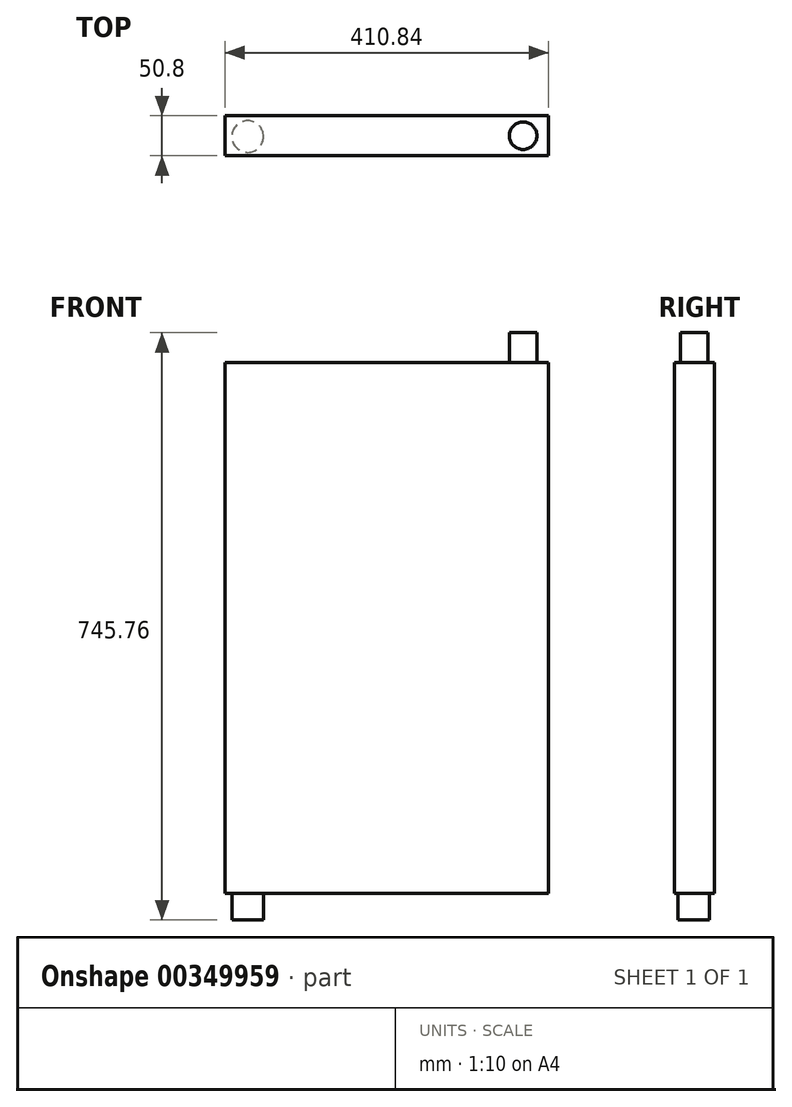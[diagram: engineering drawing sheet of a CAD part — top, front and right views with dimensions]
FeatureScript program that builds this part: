
annotation { "Feature Type Name" : "Feature", "Feature Type Description" : "" }
export const myFeature = defineFeature(function(context is Context, id is Id, definition is map)
    precondition{}
    {
        {
            var Q0;
            Q0=qCreatedBy(makeId("Front.planeOp"),FACE);
            var sketch = newSketch(context, id + "F0", { "sketchPlane" : qUnion([Q0])});
            skLineSegment(sketch, "E0.bottom", {"start": v(205.42, -336.94) * mm, "end": v(-205.42, -336.94) * mm});
            skLineSegment(sketch, "E0.top", {"start": v(205.42, 336.94) * mm, "end": v(-205.42, 336.94) * mm});
            skLineSegment(sketch, "E0.left", {"start": v(205.42, -336.94) * mm, "end": v(205.42, 336.94) * mm});
            skLineSegment(sketch, "E0.right", {"start": v(-205.42, -336.94) * mm, "end": v(-205.42, 336.94) * mm});
            skPoint(sketch, "E0.middle", {"position": v(0, 0) * mm});
            skSolve(sketch);
        }
        {
            var Q0;
            Q0 = qSketchRegion(id + "F0", true);
            extrude(context, id + "F1", {"entities" : qUnion([Q0]), "depth" : 50.8 * mm});
        }
        {
            var Q0;
            Q0=makeQuery(id+"F1.opExtrude","SWEPT_FACE",FACE,{"disambiguationData":[OSD([sQuery(id+"F0.wireOp",EDGE,"E0.bottom")])]});
            var sketch = newSketch(context, id + "F2", { "sketchPlane" : qUnion([Q0])});
            skCircle(sketch, "E1", {"center": v(-176.62, 26.48) * mm, "radius": 20.1 * mm});
            skSolve(sketch);
        }
        {
            var Q0;
            Q0 = qSketchRegion(id + "F2", true);
            extrude(context, id + "F3", {"entities" : qUnion([Q0]), "operationType" : NewBodyOperationType.ADD, "depth" : 33.78 * mm});
        }
        {
            var Q0;
            Q0=makeQuery(id+"F1.opExtrude","SWEPT_FACE",FACE,{"disambiguationData":[OSD([sQuery(id+"F0.wireOp",EDGE,"E0.top")])]});
            var sketch = newSketch(context, id + "F4", { "sketchPlane" : qUnion([Q0])});
            skCircle(sketch, "E2", {"center": v(173.23, -25.4) * mm, "radius": 17.47 * mm});
            skPoint(sketch, "E2.centerSnap0", {"position": v(-205.42, -25.4) * mm});
            skSolve(sketch);
        }
        {
            var Q0;
            Q0 = qSketchRegion(id + "F4", true);
            extrude(context, id + "F5", {"entities" : qUnion([Q0]), "operationType" : NewBodyOperationType.ADD, "depth" : 38.1 * mm});
        }
    });
